# Revit family: Gira_104000
name_source: partatom
category: Electrical Fixtures
revit_build: Autodesk Revit 2017 (Build: 20160225_1515(x64)
units: mm (PartAtom-declared; Revit-internal decimal feet)

## family parameters
Cut with Voids When Loaded = No
Host = Face
Maintain Annotation Orientation = No
Part Type = Normal
Room Calculation Point = No
Round Connector Dimension = Use Diameter
Shared = No

## types (1)
- Swit.act. 2-g 16 A man.act. KNX DRA
    BIM = https://media.live.bim.site 8f.rfa
    BIMSITE_PRODUCT_ID = 39b9523d5bf61837385f41dbcf1c51630087c11a
    Bus connection included = Yes
    Cost = 0 $
    Default Elevation = 1219 mm
    Description = Swit.act.2g 16A DRA KNX KNX switching actuator, 2-gang 16 A with manual actuation,DRA plus DRA switching actuators with integrated bus coupler. For switching independently controllable groups of loads. With manual switch for switching over the relay (On Off) parallel or without KNX operation. Multi-phase connection. No additional power supply required.,Features: - Manual actuation of the relay independent of the bus or switching position indication. - NO contact or NC contact operation. - Central switching function. - Group feedback for reduction of bus load. - Active or passive (object can be read out) cyclical feedback function. - Feedback can be delayed until after the recovery of bus voltage. - Logical linking function for each output. - Block function can be parameterised for each channel. As an alternative, forced setting function for each output. - Time functions (switch-on off delay, staircase light function – also with advance warning function). - Integration in light scenes is possible, eight internal scenes at the most can be parameterised per channel. - Memory function for light scenes. - Elapsed operating time meter as forward backward counter with limit function (limit can be changed via bus) can be activated for each output. - Input monitoring for cyclical updating with safety setting. - Reactions in case of bus voltage failure and restoration can be set for each channel following an ETS programming process. - Independent switching of the two outputs.,Notes : - Installation on DIN top-hat rail. - VDE approval in accordance with EN 60669-1, EN 60669-2-1.
    GTIN = 4010337058359
    HAN = 104000
    HeinzeBIM = https://www.heinze.de
    Local operation/hand operation = Yes
    Manufacturer = Gira
    Max. number of venetian-blind outputs = 0
    Number of binary inputs = 0
    Number of inputs = 0
    Number of outputs = 0
    Suitable for C-load = No
    URL = https://www.gira.de
    With switch function = No

## geometry (parser evidence)
native form markers: Blend x2, Sweep x3
no freeform markers — native parametric forms only
